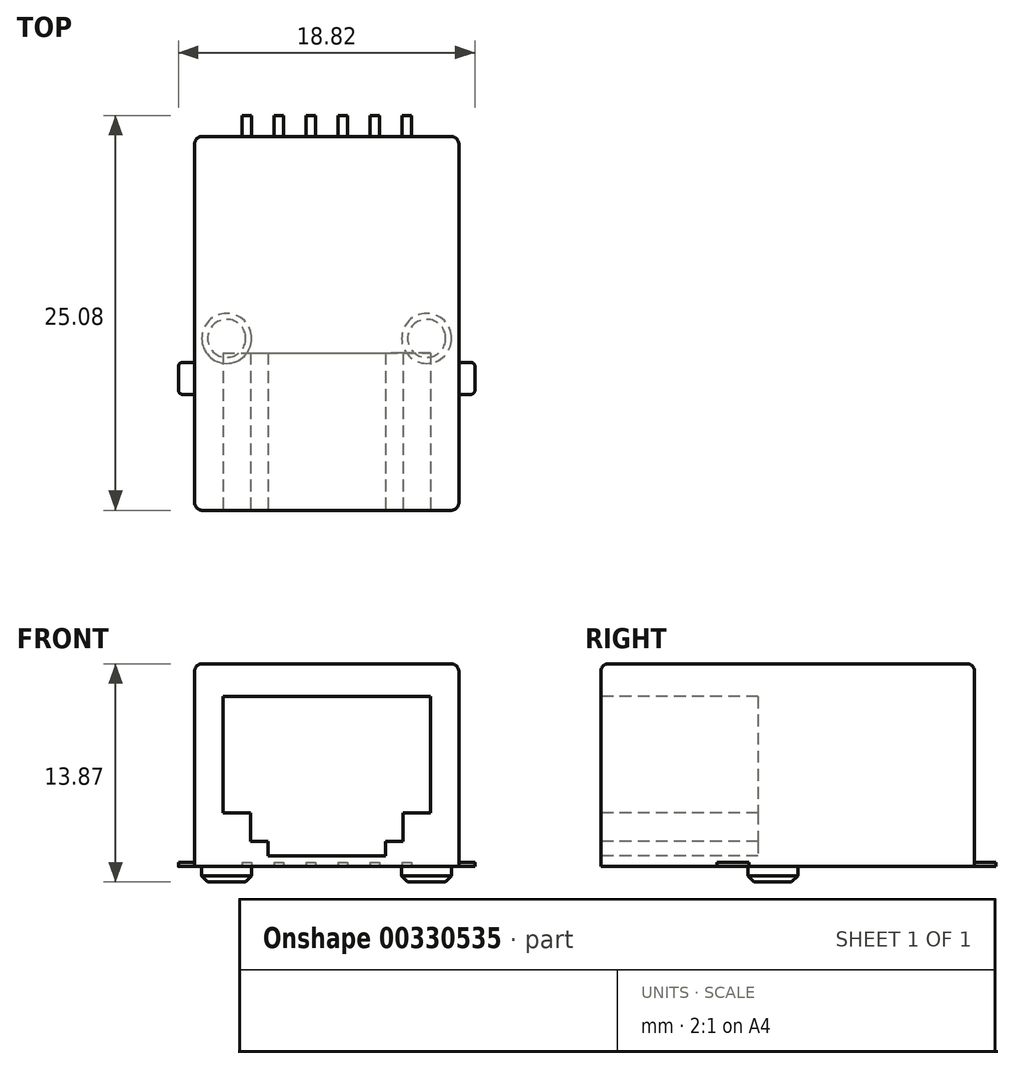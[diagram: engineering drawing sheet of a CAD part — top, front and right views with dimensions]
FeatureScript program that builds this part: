
annotation { "Feature Type Name" : "Feature", "Feature Type Description" : "" }
export const myFeature = defineFeature(function(context is Context, id is Id, definition is map)
    precondition{}
    {
        {
            var Q0;
            Q0=qCreatedBy(makeId("Top.planeOp"),FACE);
            var sketch = newSketch(context, id + "F0", { "sketchPlane" : qUnion([Q0])});
            skLineSegment(sketch, "E0.bottom", {"start": v(8.4, -11.87) * mm, "end": v(-8.4, -11.87) * mm});
            skLineSegment(sketch, "E0.top", {"start": v(8.4, 11.87) * mm, "end": v(-8.4, 11.87) * mm});
            skLineSegment(sketch, "E0.left", {"start": v(8.4, -11.87) * mm, "end": v(8.4, 11.87) * mm});
            skLineSegment(sketch, "E0.right", {"start": v(-8.4, -11.87) * mm, "end": v(-8.4, 11.87) * mm});
            skPoint(sketch, "E0.middle", {"position": v(0, 0) * mm});
            skSolve(sketch);
        }
        {
            var Q0;
            Q0=qSketchRegion(id+"F0",true);
            extrude(context, id + "F1", {"entities" : qUnion([Q0]), "depth" : 12.88 * mm, "offsetDistance" : 25 * mm});
        }
        {
            var Q0;
            Q0=makeQuery(id+"FJxkkNZS4rezTmz_1.boolean.opBoolean","MERGE",EDGE,{"derivedFrom":[makeQuery(id+"F1.opExtrude","SWEPT_EDGE",EDGE,{"disambiguationData":[OSD([sQuery(id+"F0.wireOp",EDGE,"E0.bottom"),sQuery(id+"F0.wireOp",EDGE,"E0.right")])]}),makeQuery(id+"FJxkkNZS4rezTmz_1.opExtrude","SWEPT_EDGE",EDGE,{"disambiguationData":[OSD([sQuery(id+"F9NPPUefej9rEKj_1.wireOp",EDGE,"desPq1yY-o5Qy-SBm8-Lvxq-VWqHqrpmvovc.bottom"),sQuery(id+"F9NPPUefej9rEKj_1.wireOp",EDGE,"desPq1yY-o5Qy-SBm8-Lvxq-VWqHqrpmvovc.right")])]})]});
            var Q1;
            Q1=makeQuery(id+"FJxkkNZS4rezTmz_1.boolean.opBoolean","MERGE",EDGE,{"derivedFrom":[makeQuery(id+"F1.opExtrude","SWEPT_EDGE",EDGE,{"disambiguationData":[OSD([sQuery(id+"F0.wireOp",EDGE,"E0.bottom"),sQuery(id+"F0.wireOp",EDGE,"E0.left")])]}),makeQuery(id+"FJxkkNZS4rezTmz_1.opExtrude","SWEPT_EDGE",EDGE,{"disambiguationData":[OSD([sQuery(id+"F9NPPUefej9rEKj_1.wireOp",EDGE,"desPq1yY-o5Qy-SBm8-Lvxq-VWqHqrpmvovc.bottom"),sQuery(id+"F9NPPUefej9rEKj_1.wireOp",EDGE,"desPq1yY-o5Qy-SBm8-Lvxq-VWqHqrpmvovc.left")])]})]});
            var Q2;
            Q2=makeQuery(id+"F1.opExtrude","SWEPT_EDGE",EDGE,{"disambiguationData":[OSD([sQuery(id+"F0.wireOp",EDGE,"E0.top"),sQuery(id+"F0.wireOp",EDGE,"E0.left")])]});
            var Q3;
            Q3=makeQuery(id+"F1.opExtrude","SWEPT_EDGE",EDGE,{"disambiguationData":[OSD([sQuery(id+"F0.wireOp",EDGE,"E0.top"),sQuery(id+"F0.wireOp",EDGE,"E0.right")])]});
            var Q4;
            Q4=makeQuery(id+"F1.opExtrude","CAP_EDGE",EDGE,{"disambiguationData":[OSD([sQuery(id+"F0.wireOp",EDGE,"E0.bottom")])],"isStart":false});
            var Q5;
            Q5=makeQuery(id+"F1.opExtrude","CAP_EDGE",EDGE,{"disambiguationData":[OSD([sQuery(id+"F0.wireOp",EDGE,"E0.right")])],"isStart":false});
            var Q6;
            Q6=makeQuery(id+"F1.opExtrude","CAP_EDGE",EDGE,{"disambiguationData":[OSD([sQuery(id+"F0.wireOp",EDGE,"E0.top")])],"isStart":false});
            var Q7;
            Q7=makeQuery(id+"F1.opExtrude","CAP_EDGE",EDGE,{"disambiguationData":[OSD([sQuery(id+"F0.wireOp",EDGE,"E0.left")])],"isStart":false});
            var Q8;
            Q8=makeQuery(id+"FJxkkNZS4rezTmz_1.opExtrude","CAP_EDGE",EDGE,{"disambiguationData":[OSD([sQuery(id+"F9NPPUefej9rEKj_1.wireOp",EDGE,"desPq1yY-o5Qy-SBm8-Lvxq-VWqHqrpmvovc.bottom")])],"isStart":false});
            var Q9;
            Q9=makeQuery(id+"FJxkkNZS4rezTmz_1.opExtrude","CAP_EDGE",EDGE,{"disambiguationData":[OSD([sQuery(id+"F9NPPUefej9rEKj_1.wireOp",EDGE,"desPq1yY-o5Qy-SBm8-Lvxq-VWqHqrpmvovc.right")])],"isStart":false});
            var Q10;
            Q10=makeQuery(id+"FJxkkNZS4rezTmz_1.opExtrude","CAP_EDGE",EDGE,{"disambiguationData":[OSD([sQuery(id+"F9NPPUefej9rEKj_1.wireOp",EDGE,"desPq1yY-o5Qy-SBm8-Lvxq-VWqHqrpmvovc.left")])],"isStart":false});
            fillet(context, id + "F2", {"entities" : qUnion([Q0, Q1, Q2, Q3, Q4, Q5, Q6, Q7, Q8, Q9, Q10]), "radius" : .5 * mm, "tangentPropagation" : true, "allowEdgeOverflow" : false});
        }
        {
            var Q0;
            Q0=makeQuery(id+"FJxkkNZS4rezTmz_1.boolean.opBoolean","MERGE",FACE,{"derivedFrom":[makeQuery(id+"F1.opExtrude","SWEPT_FACE",FACE,{"disambiguationData":[OSD([sQuery(id+"F0.wireOp",EDGE,"E0.bottom")])]}),makeQuery(id+"FJxkkNZS4rezTmz_1.opExtrude","SWEPT_FACE",FACE,{"disambiguationData":[OSD([sQuery(id+"F9NPPUefej9rEKj_1.wireOp",EDGE,"desPq1yY-o5Qy-SBm8-Lvxq-VWqHqrpmvovc.bottom")])]})]});
            var sketch = newSketch(context, id + "F3", { "sketchPlane" : qUnion([Q0])});
            skLineSegment(sketch, "E1", {"start": v(0, 12.94) * mm, "end": v(0, 0) * mm, "construction": true});
            skLineSegment(sketch, "E2", {"start": v(0, 10.8) * mm, "end": v(-6.59, 10.8) * mm});
            skLineSegment(sketch, "E3", {"start": v(-6.59, 10.8) * mm, "end": v(-6.59, 3.41) * mm});
            skLineSegment(sketch, "E4", {"start": v(-6.59, 3.41) * mm, "end": v(-4.85, 3.41) * mm});
            skLineSegment(sketch, "E5", {"start": v(-4.85, 3.41) * mm, "end": v(-4.85, 1.6) * mm});
            skLineSegment(sketch, "E6", {"start": v(-4.85, 1.6) * mm, "end": v(-3.73, 1.6) * mm});
            skLineSegment(sketch, "E7", {"start": v(-3.73, 1.6) * mm, "end": v(-3.73, 0.68) * mm});
            skLineSegment(sketch, "E8", {"start": v(-3.73, 0.68) * mm, "end": v(0, 0.68) * mm});
            skLineSegment(sketch, "E9.MirrorCS", {"start": v(4.85, 1.6) * mm, "end": v(3.73, 1.6) * mm});
            skLineSegment(sketch, "E10.MirrorCS", {"start": v(3.73, 1.6) * mm, "end": v(3.73, 0.68) * mm});
            skLineSegment(sketch, "E11.MirrorCS", {"start": v(6.59, 3.41) * mm, "end": v(4.85, 3.41) * mm});
            skLineSegment(sketch, "E12.MirrorCS", {"start": v(4.85, 3.41) * mm, "end": v(4.85, 1.6) * mm});
            skLineSegment(sketch, "E13.MirrorCS", {"start": v(0, 10.8) * mm, "end": v(6.59, 10.8) * mm});
            skLineSegment(sketch, "E14.MirrorCS", {"start": v(3.73, 0.68) * mm, "end": v(0, 0.68) * mm});
            skLineSegment(sketch, "E15.MirrorCS", {"start": v(6.59, 10.8) * mm, "end": v(6.59, 3.41) * mm});
            skSolve(sketch);
        }
        {
            var Q0;
            Q0=qSketchRegion(id+"F3",true);
            extrude(context, id + "F4", {"entities" : qUnion([Q0]), "operationType" : NewBodyOperationType.REMOVE, "oppositeDirection" : true, "depth" : 10 * mm, "offsetDistance" : 25 * mm});
        }
        {
            var Q0;
            Q0=makeQuery(id+"F1.opExtrude","CAP_FACE",FACE,{"disambiguationData":[OSD([sQuery(id+"F0.wireOp",EDGE,"E0.bottom"),sQuery(id+"F0.wireOp",EDGE,"E0.top"),sQuery(id+"F0.wireOp",EDGE,"E0.left"),sQuery(id+"F0.wireOp",EDGE,"E0.right")])],"isStart":true});
            var sketch = newSketch(context, id + "F5", { "sketchPlane" : qUnion([Q0])});
            skCircle(sketch, "E16", {"center": v(6.35, 0.95) * mm, "radius": 1.59 * mm});
            skLineSegment(sketch, "E17", {"start": v(0, 11.87) * mm, "end": v(0, -11.87) * mm, "construction": true});
            skCircle(sketch, "E18.MirrorC", {"center": v(-6.35, 0.95) * mm, "radius": 1.59 * mm});
            skSolve(sketch);
        }
        {
            var Q0;
            Q0=qSketchRegion(id+"F5",true);
            extrude(context, id + "F6", {"entities" : qUnion([Q0]), "operationType" : NewBodyOperationType.ADD, "depth" : 1 * mm, "offsetDistance" : 25.4 * mm});
        }
        {
            var Q0;
            Q0=makeQuery(id+"F1.opExtrude","CAP_FACE",FACE,{"disambiguationData":[OSD([sQuery(id+"F0.wireOp",EDGE,"E0.bottom"),sQuery(id+"F0.wireOp",EDGE,"E0.top"),sQuery(id+"F0.wireOp",EDGE,"E0.left"),sQuery(id+"F0.wireOp",EDGE,"E0.right")])],"isStart":true});
            var sketch = newSketch(context, id + "F7", { "sketchPlane" : qUnion([Q0])});
            skLineSegment(sketch, "E19", {"start": v(0, -11.87) * mm, "end": v(0, 11.87) * mm, "construction": true});
            skLineSegment(sketch, "E20.bottom", {"start": v(0.71, -11.81) * mm, "end": v(1.32, -11.81) * mm});
            skLineSegment(sketch, "E20.top", {"start": v(0.71, -13.2) * mm, "end": v(1.32, -13.2) * mm});
            skLineSegment(sketch, "E20.left", {"start": v(0.71, -11.81) * mm, "end": v(0.71, -13.2) * mm});
            skLineSegment(sketch, "E20.right", {"start": v(1.32, -11.81) * mm, "end": v(1.32, -13.2) * mm});
            skPoint(sketch, "E20.middle", {"position": v(1.02, -12.5) * mm});
            skLineSegment(sketch, "E21.1.0.0", {"start": v(3.35, -11.81) * mm, "end": v(3.35, -13.2) * mm});
            skLineSegment(sketch, "E21.1.0.1", {"start": v(2.74, -13.2) * mm, "end": v(3.35, -13.2) * mm});
            skLineSegment(sketch, "E21.1.0.2", {"start": v(2.74, -11.81) * mm, "end": v(2.74, -13.2) * mm});
            skPoint(sketch, "E21.1.0.3", {"position": v(3.05, -12.5) * mm});
            skLineSegment(sketch, "E21.1.0.4", {"start": v(2.74, -11.81) * mm, "end": v(3.35, -11.81) * mm});
            skLineSegment(sketch, "E21.2.0.0", {"start": v(5.38, -11.81) * mm, "end": v(5.38, -13.2) * mm});
            skLineSegment(sketch, "E21.2.0.1", {"start": v(4.78, -13.2) * mm, "end": v(5.38, -13.2) * mm});
            skLineSegment(sketch, "E21.2.0.2", {"start": v(4.78, -11.81) * mm, "end": v(4.78, -13.2) * mm});
            skPoint(sketch, "E21.2.0.3", {"position": v(5.08, -12.5) * mm});
            skLineSegment(sketch, "E21.2.0.4", {"start": v(4.78, -11.81) * mm, "end": v(5.38, -11.81) * mm});
            skLineSegment(sketch, "E21.direction1", {"start": v(0.71, -13.2) * mm, "end": v(2.74, -13.2) * mm, "construction": true});
            skLineSegment(sketch, "E22.MirrorCS", {"start": v(-0.71, -13.2) * mm, "end": v(-1.32, -13.2) * mm});
            skLineSegment(sketch, "E23.MirrorCS", {"start": v(-4.78, -11.81) * mm, "end": v(-5.38, -11.81) * mm});
            skLineSegment(sketch, "E24.MirrorCS", {"start": v(-2.74, -11.81) * mm, "end": v(-3.35, -11.81) * mm});
            skLineSegment(sketch, "E25.MirrorCS", {"start": v(-2.74, -13.2) * mm, "end": v(-3.35, -13.2) * mm});
            skLineSegment(sketch, "E26.MirrorCS", {"start": v(-0.71, -13.2) * mm, "end": v(-2.74, -13.2) * mm, "construction": true});
            skLineSegment(sketch, "E27.MirrorCS", {"start": v(-0.71, -11.81) * mm, "end": v(-1.32, -11.81) * mm});
            skLineSegment(sketch, "E28.MirrorCS", {"start": v(-4.78, -13.2) * mm, "end": v(-5.38, -13.2) * mm});
            skLineSegment(sketch, "E29.MirrorCS", {"start": v(-5.38, -11.81) * mm, "end": v(-5.38, -13.2) * mm});
            skLineSegment(sketch, "E30.MirrorCS", {"start": v(-2.74, -11.81) * mm, "end": v(-2.74, -13.2) * mm});
            skPoint(sketch, "E31.MirrorP", {"position": v(-5.08, -12.5) * mm});
            skLineSegment(sketch, "E32.MirrorCS", {"start": v(-4.78, -11.81) * mm, "end": v(-4.78, -13.2) * mm});
            skPoint(sketch, "E33.MirrorP", {"position": v(-1.02, -12.5) * mm});
            skPoint(sketch, "E34.MirrorP", {"position": v(-3.05, -12.5) * mm});
            skLineSegment(sketch, "E35.MirrorCS", {"start": v(-0.71, -11.81) * mm, "end": v(-0.71, -13.2) * mm});
            skLineSegment(sketch, "E36.MirrorCS", {"start": v(-3.35, -11.81) * mm, "end": v(-3.35, -13.2) * mm});
            skLineSegment(sketch, "E37.MirrorCS", {"start": v(-1.32, -11.81) * mm, "end": v(-1.32, -13.2) * mm});
            skLineSegment(sketch, "E38.bottom", {"start": v(8.4, 4.5) * mm, "end": v(9.16, 4.5) * mm});
            skLineSegment(sketch, "E38.top", {"start": v(8.4, 2.48) * mm, "end": v(9.16, 2.48) * mm});
            skLineSegment(sketch, "E38.left", {"start": v(8.4, 4.5) * mm, "end": v(8.4, 2.48) * mm});
            skLineSegment(sketch, "E38.right", {"start": v(9.41, 4.25) * mm, "end": v(9.41, 2.73) * mm});
            skPoint(sketch, "E38.middle", {"position": v(8.9, 3.5) * mm});
            skPoint(sketch, "E39.visualSharp", {"position": v(9.41, 2.48) * mm});
            skArc(sketch, "E39.filletArc", {"start": v(9.16, 2.48) * mm, "mid": v(9.34, 2.55) * mm, "end": v(9.41, 2.73) * mm});
            skPoint(sketch, "E40.visualSharp", {"position": v(9.41, 4.5) * mm});
            skArc(sketch, "E40.filletArc", {"start": v(9.41, 4.25) * mm, "mid": v(9.34, 4.43) * mm, "end": v(9.16, 4.5) * mm});
            skArc(sketch, "E41.MirrorCS", {"start": v(-9.41, 4.25) * mm, "mid": v(-9.34, 4.43) * mm, "end": v(-9.16, 4.5) * mm});
            skArc(sketch, "E42.MirrorCS", {"start": v(-9.16, 2.48) * mm, "mid": v(-9.34, 2.55) * mm, "end": v(-9.41, 2.73) * mm});
            skLineSegment(sketch, "E43.MirrorCS", {"start": v(-9.41, 4.25) * mm, "end": v(-9.41, 2.73) * mm});
            skLineSegment(sketch, "E44.MirrorCS", {"start": v(-8.4, 4.5) * mm, "end": v(-8.4, 2.48) * mm});
            skLineSegment(sketch, "E45.MirrorCS", {"start": v(-8.4, 4.5) * mm, "end": v(-9.16, 4.5) * mm});
            skPoint(sketch, "E46.MirrorP", {"position": v(-9.41, 4.5) * mm});
            skLineSegment(sketch, "E47.MirrorCS", {"start": v(-8.4, 2.48) * mm, "end": v(-9.16, 2.48) * mm});
            skPoint(sketch, "E48.MirrorP", {"position": v(-9.41, 2.48) * mm});
            skPoint(sketch, "E49.MirrorP", {"position": v(-8.9, 3.5) * mm});
            skSolve(sketch);
        }
        {
            var Q0;
            Q0=qSketchRegion(id+"F7",true);
            extrude(context, id + "F8", {"entities" : qUnion([Q0]), "operationType" : NewBodyOperationType.ADD, "oppositeDirection" : true, "depth" : 0.25 * mm, "offsetDistance" : 25.4 * mm});
        }
        {
            var Q0;
            Q0=makeQuery(id+"F6.opExtrude","CAP_EDGE",EDGE,{"disambiguationData":[OSD([sQuery(id+"F5.wireOp",EDGE,"E16")])],"isStart":false});
            var Q1;
            Q1=makeQuery(id+"F6.opExtrude","CAP_EDGE",EDGE,{"disambiguationData":[OSD([sQuery(id+"F5.wireOp",EDGE,"E18.MirrorC")])],"isStart":false});
            chamfer(context, id + "F9", {"entities" : qUnion([Q0, Q1]), "width" : 0.38 * mm, "tangentPropagation" : true});
        }
    });
